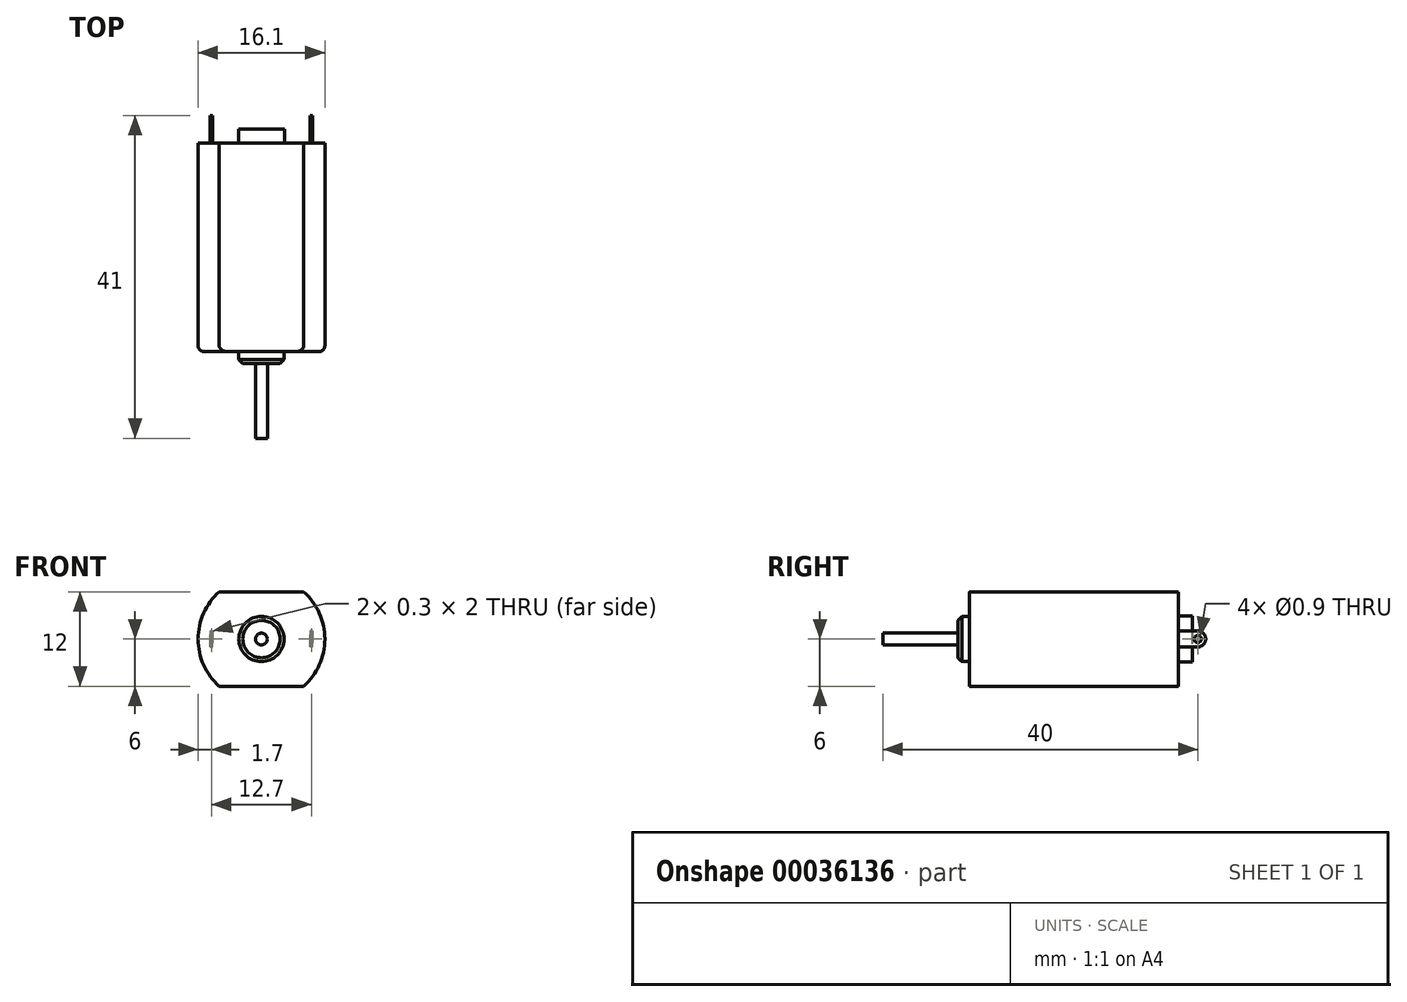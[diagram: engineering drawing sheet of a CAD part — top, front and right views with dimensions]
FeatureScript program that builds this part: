
annotation { "Feature Type Name" : "Feature", "Feature Type Description" : "" }
export const myFeature = defineFeature(function(context is Context, id is Id, definition is map)
    precondition{}
    {
        {
            var Q0;
            Q0=qCreatedBy(makeId("Front.planeOp"),FACE);
            var sketch = newSketch(context, id + "F0", { "sketchPlane" : qUnion([Q0])});
            skCircle(sketch, "E0", {"center": v(0, 0) * mm, "radius": 8.05 * mm});
            skSolve(sketch);
        }
        {
            var Q0;
            Q0=qSketchRegion(id+"F0",true);
            var Q1;
            Q1=sQuery(id+"F0.wireOp",EDGE,"E0");
            extrude(context, id + "F1", {"entities" : qUnion([Q0]), "surfaceEntities" : qUnion([Q1]), "oppositeDirection" : true, "depth" : 26.5 * mm});
        }
        {
            var Q0;
            Q0=makeQuery(id+"F1.opExtrude","CAP_FACE",FACE,{"disambiguationData":[OSD([sQuery(id+"F0.wireOp",EDGE,"E0")])],"isStart":true});
            var sketch = newSketch(context, id + "F2", { "sketchPlane" : qUnion([Q0])});
            skLineSegment(sketch, "E1", {"start": v(-5.37, 6) * mm, "end": v(5.37, 6) * mm});
            skLineSegment(sketch, "E2", {"start": v(-5.37, -6) * mm, "end": v(5.37, -6) * mm});
            skArc(sketch, "E3", {"start": v(5.37, 6) * mm, "mid": v(0, 8.05) * mm, "end": v(-5.37, 6) * mm});
            skArc(sketch, "E4", {"start": v(-5.37, -6) * mm, "mid": v(0, -8.05) * mm, "end": v(5.37, -6) * mm});
            skSolve(sketch);
        }
        {
            var Q0;
            Q0=qSketchRegion(id+"F2",true);
            extrude(context, id + "F3", {"entities" : qUnion([Q0]), "operationType" : NewBodyOperationType.REMOVE, "endBound" : BoundingType.UP_TO_NEXT, "oppositeDirection" : true, "depth" : 25 * mm});
        }
        {
            var Q0;
            Q0=qCreatedBy(makeId("Front.planeOp"),FACE);
            var sketch = newSketch(context, id + "F4", { "sketchPlane" : qUnion([Q0])});
            skCircle(sketch, "E5", {"center": v(0, 0) * mm, "radius": 2.87 * mm});
            skSolve(sketch);
        }
        {
            var Q0;
            Q0=makeQuery(id+"F1.opExtrude","CAP_FACE",FACE,{"disambiguationData":[OSD([sQuery(id+"F0.wireOp",EDGE,"E0")])],"isStart":true});
            var sketch = newSketch(context, id + "F5", { "sketchPlane" : qUnion([Q0])});
            skCircle(sketch, "E6", {"center": v(0, 0) * mm, "radius": 0.75 * mm});
            skSolve(sketch);
        }
        {
            var Q0;
            Q0=qSketchRegion(id+"F5",true);
            extrude(context, id + "F6", {"entities" : qUnion([Q0]), "operationType" : NewBodyOperationType.ADD, "depth" : 11 * mm});
        }
        {
            var Q0;
            Q0=qSketchRegion(id+"F4",true);
            extrude(context, id + "F7", {"entities" : qUnion([Q0]), "operationType" : NewBodyOperationType.ADD, "depth" : 1.5 * mm});
        }
        {
            var Q0;
            Q0=qSketchRegion(id+"F4",true);
            extrude(context, id + "F8", {"entities" : qUnion([Q0]), "operationType" : NewBodyOperationType.ADD, "depth" : 1.5 * mm});
        }
        {
            var Q0;
            Q0=makeQuery(id+"F1.opExtrude","CAP_FACE",FACE,{"disambiguationData":[OSD([sQuery(id+"F0.wireOp",EDGE,"E0")])],"isStart":false});
            var sketch = newSketch(context, id + "F9", { "sketchPlane" : qUnion([Q0])});
            skCircle(sketch, "E7", {"center": v(0, 0) * mm, "radius": 2.93 * mm});
            skSolve(sketch);
        }
        {
            var Q0;
            Q0=qSketchRegion(id+"F9",true);
            extrude(context, id + "F10", {"entities" : qUnion([Q0]), "operationType" : NewBodyOperationType.ADD, "depth" : 1.8 * mm});
        }
        {
            var Q0;
            Q0=qCreatedBy(makeId("Right.planeOp"),FACE);
            cPlane(context, id + "F11", {"entities" : qUnion([Q0]), "cplaneType" : CPlaneType.OFFSET, "offset" : 6.2 * mm, "width" : 150 * mm, "height" : 150 * mm});
        }
        {
            var Q0;
            Q0=qCreatedBy(id+"F11.planeOp",FACE);
            var sketch = newSketch(context, id + "F12", { "sketchPlane" : qUnion([Q0])});
            skLineSegment(sketch, "E8", {"start": v(29, 1) * mm, "end": v(26.5, 1) * mm});
            skLineSegment(sketch, "E9", {"start": v(26.5, 1) * mm, "end": v(26.5, -1) * mm});
            skLineSegment(sketch, "E10", {"start": v(26.5, -1) * mm, "end": v(29, -1) * mm});
            skArc(sketch, "E11", {"start": v(29, -1) * mm, "mid": v(30, 0) * mm, "end": v(29, 1) * mm});
            skCircle(sketch, "E12", {"center": v(29, 0) * mm, "radius": 0.45 * mm});
            skSolve(sketch);
        }
        {
            var Q0;
            Q0=makeQuery(id+"F12.imprint","IMPRINT",FACE,{"disambiguationData":[TD([[makeQuery(id+"F12.imprint","IMPRINT",EDGE,{"derivedFrom":sQuery(id+"F12.wireOp",EDGE,"E8")}),1.0]])]});
            extrude(context, id + "F13", {"entities" : qUnion([Q0]), "depth" : 0.3 * mm});
        }
        {
            var Q0;
            Q0=makeQuery(id+"F13.opExtrude","SWEPT_BODY",BODY,{"disambiguationData":[OSD([sQuery(id+"F12.wireOp",EDGE,"E8"),sQuery(id+"F12.wireOp",EDGE,"E9"),sQuery(id+"F12.wireOp",EDGE,"E10"),sQuery(id+"F12.wireOp",EDGE,"E11"),sQuery(id+"F12.wireOp",EDGE,"E12")])]});
            var Q1;
            Q1=qCreatedBy(makeId("Right.planeOp"),FACE);
            mirror(context, id + "F14", {"operationType" : NewBodyOperationType.ADD, "entities" : qUnion([Q0]), "mirrorPlane" : qUnion([Q1])});
        }
        {
            var Q0;
            Q0=makeQuery(id+"F3.boolean.opBoolean","COPY",EDGE,{"derivedFrom":makeQuery(id+"F3.opExtrude","CAP_EDGE",EDGE,{"disambiguationData":[OSD([sQuery(id+"F2.wireOp",EDGE,"E1")])],"isStart":true})});
            var Q1;
            Q1=makeQuery(id+"F3.boolean.opBoolean","SPLIT",EDGE,{"disambiguationData":[OD(1.0)],"derivedFrom":makeQuery(id+"F1.opExtrude","CAP_EDGE",EDGE,{"disambiguationData":[OSD([sQuery(id+"F0.wireOp",EDGE,"E0")])],"isStart":true})});
            var Q2;
            Q2=makeQuery(id+"F3.boolean.opBoolean","COPY",EDGE,{"derivedFrom":makeQuery(id+"F3.opExtrude","CAP_EDGE",EDGE,{"disambiguationData":[OSD([sQuery(id+"F2.wireOp",EDGE,"E2")])],"isStart":true})});
            var Q3;
            Q3=makeQuery(id+"F3.boolean.opBoolean","SPLIT",EDGE,{"disambiguationData":[OD(0.0)],"derivedFrom":makeQuery(id+"F1.opExtrude","CAP_EDGE",EDGE,{"disambiguationData":[OSD([sQuery(id+"F0.wireOp",EDGE,"E0")])],"isStart":true})});
            fillet(context, id + "F15", {"entities" : qUnion([Q0, Q1, Q2, Q3]), "radius" : 0.75 * mm, "tangentPropagation" : true, "allowEdgeOverflow" : false});
        }
        {
            var Q0;
            Q0=makeQuery(id+"F7.opExtrude","CAP_EDGE",EDGE,{"disambiguationData":[OSD([sQuery(id+"F4.wireOp",EDGE,"E5")])],"isStart":false});
            chamfer(context, id + "F16", {"entities" : qUnion([Q0]), "width" : 0.5 * mm, "tangentPropagation" : true});
        }
        {
            var Q0;
            Q0=makeQuery(id+"F1.opExtrude","SWEPT_BODY",BODY,{"disambiguationData":[OSD([sQuery(id+"F0.wireOp",EDGE,"E0")])]});
            transform(context, id + "F17", {"entities" : qUnion([Q0]), "transformType" : TransformType.TRANSLATION_3D, "dx" : 0 * mm, "dy" : 0 * mm, "dz" : 0 * mm, "makeCopy" : true});
        }
    });
